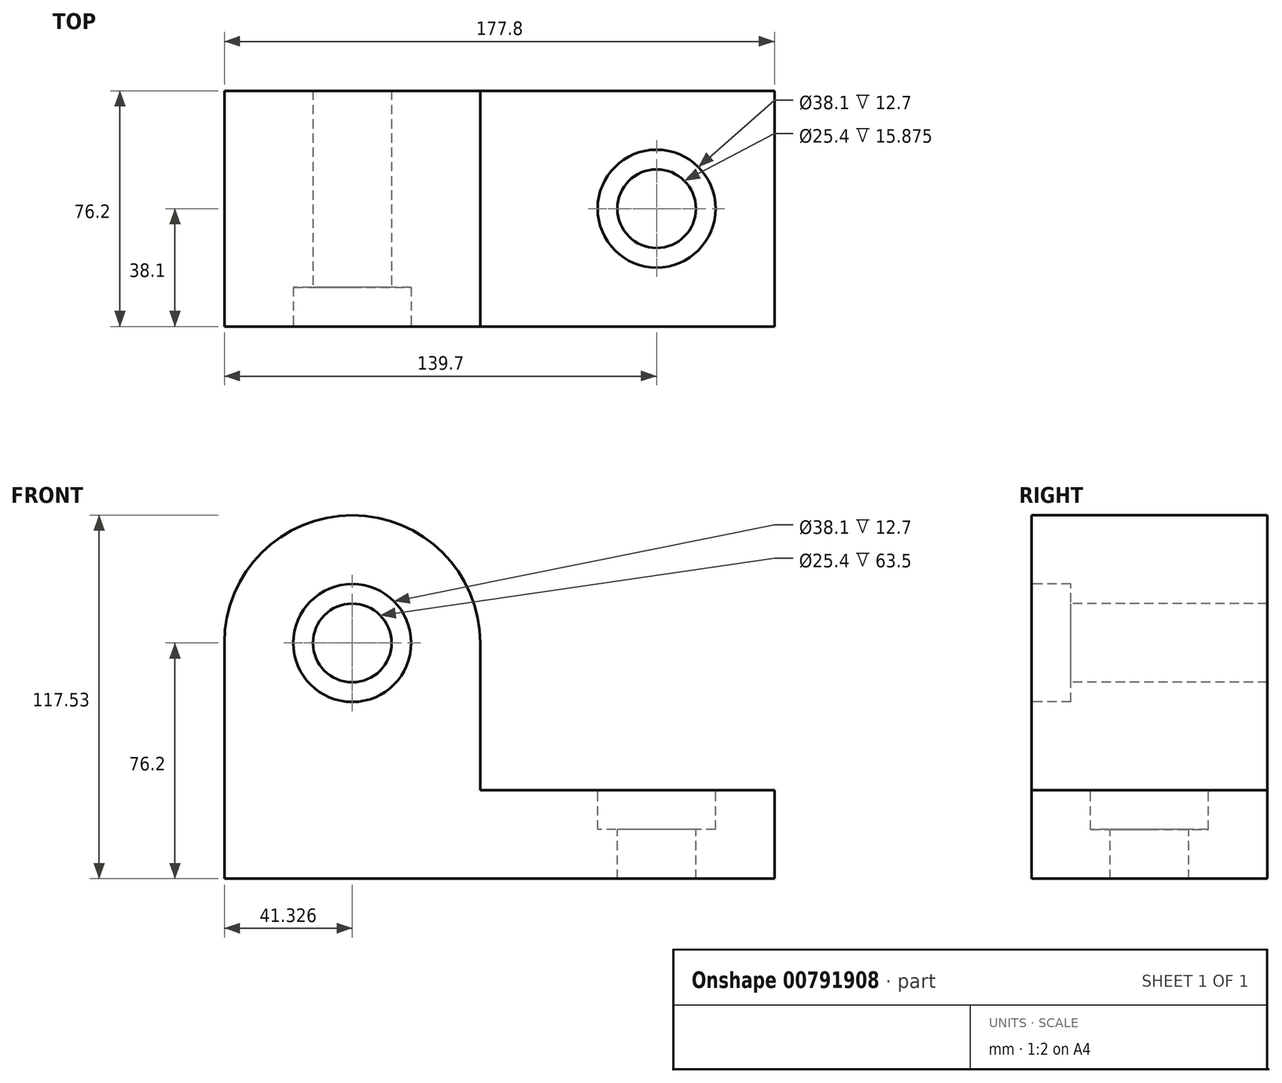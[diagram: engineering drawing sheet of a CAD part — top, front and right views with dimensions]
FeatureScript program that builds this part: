
annotation { "Feature Type Name" : "Feature", "Feature Type Description" : "" }
export const myFeature = defineFeature(function(context is Context, id is Id, definition is map)
    precondition{}
    {
        {
            var Q0;
            Q0=qCreatedBy(makeId("Front.planeOp"),FACE);
            var sketch = newSketch(context, id + "F0", { "sketchPlane" : qUnion([Q0])});
            skLineSegment(sketch, "E0", {"start": v(0, 0) * mm, "end": v(177.8, 0) * mm});
            skLineSegment(sketch, "E1", {"start": v(0, 0) * mm, "end": v(0, 139.7) * mm});
            skLineSegment(sketch, "E2", {"start": v(177.8, 0) * mm, "end": v(177.8, 28.58) * mm});
            skLineSegment(sketch, "E3", {"start": v(0, 0) * mm, "end": v(0, 76.2) * mm, "construction": true});
            skArc(sketch, "E4", {"start": v(82.65, 76.2) * mm, "mid": v(41.33, 117.53) * mm, "end": v(0, 76.2) * mm});
            skLineSegment(sketch, "E5", {"start": v(82.65, 76.2) * mm, "end": v(82.65, 28.58) * mm});
            skLineSegment(sketch, "E6", {"start": v(82.65, 28.58) * mm, "end": v(177.8, 28.58) * mm});
            skSolve(sketch);
        }
        {
            var Q0;
            {var subQ2=sQuery(id+"F0.wireOp",EDGE,"E0");Q0=makeQuery(id+"F0.imprint","IMPRINT",FACE,{"disambiguationData":[TD([[makeQuery(id+"F0.imprint","IMPRINT",EDGE,{"derivedFrom":subQ2}),1.0]])]});}
            extrude(context, id + "F1", {"entities" : qUnion([Q0]), "depth" : 76.2 * mm, "offsetDistance" : 25.4 * mm});
        }
        {
            var Q0;
            Q0=makeQuery(id+"F1.opExtrude","CAP_FACE",FACE,{"disambiguationData":[OSD([sQuery(id+"F0.wireOp",EDGE,"E0"),sQuery(id+"F0.wireOp",EDGE,"E1"),sQuery(id+"F0.wireOp",EDGE,"E2"),sQuery(id+"F0.wireOp",EDGE,"E4"),sQuery(id+"F0.wireOp",EDGE,"E5"),sQuery(id+"F0.wireOp",EDGE,"E6")])],"isStart":false});
            var sketch = newSketch(context, id + "F2", { "sketchPlane" : qUnion([Q0])});
            skLineSegment(sketch, "E7", {"start": v(0, 76.2) * mm, "end": v(82.65, 76.2) * mm, "construction": true});
            skLineSegment(sketch, "E8", {"start": v(41.33, 117.53) * mm, "end": v(41.33, 0) * mm, "construction": true});
            skCircle(sketch, "E9", {"center": v(41.33, 76.2) * mm, "radius": 19.05 * mm});
            skSolve(sketch);
        }
        {
            var Q0;
            Q0=makeQuery(id+"F2.imprint","IMPRINT",FACE,{"disambiguationData":[TD([[makeQuery(id+"F2.imprint","IMPRINT",EDGE,{"derivedFrom":sQuery(id+"F2.wireOp",EDGE,"E9")}),1.0]])]});
            extrude(context, id + "F3", {"entities" : qUnion([Q0]), "operationType" : NewBodyOperationType.REMOVE, "oppositeDirection" : true, "depth" : 12.7 * mm, "offsetDistance" : 25.4 * mm});
        }
        {
            var Q0;
            Q0=makeQuery(id+"F1.opExtrude","CAP_FACE",FACE,{"disambiguationData":[OSD([sQuery(id+"F0.wireOp",EDGE,"E0"),sQuery(id+"F0.wireOp",EDGE,"E1"),sQuery(id+"F0.wireOp",EDGE,"E2"),sQuery(id+"F0.wireOp",EDGE,"E4"),sQuery(id+"F0.wireOp",EDGE,"E5"),sQuery(id+"F0.wireOp",EDGE,"E6")])],"isStart":false});
            var sketch = newSketch(context, id + "F4", { "sketchPlane" : qUnion([Q0])});
            skLineSegment(sketch, "E10", {"start": v(41.33, 117.53) * mm, "end": v(41.33, 0) * mm, "construction": true});
            skLineSegment(sketch, "E11", {"start": v(0, 76.2) * mm, "end": v(82.65, 76.2) * mm, "construction": true});
            skCircle(sketch, "E12", {"center": v(41.33, 76.2) * mm, "radius": 12.7 * mm});
            skSolve(sketch);
        }
        {
            var Q0;
            Q0=makeQuery(id+"F4.imprint","IMPRINT",FACE,{"disambiguationData":[TD([[makeQuery(id+"F4.imprint","IMPRINT",EDGE,{"derivedFrom":sQuery(id+"F4.wireOp",EDGE,"E12")}),1.0]])]});
            extrude(context, id + "F5", {"entities" : qUnion([Q0]), "operationType" : NewBodyOperationType.REMOVE, "endBound" : BoundingType.UP_TO_NEXT, "oppositeDirection" : true, "depth" : 25.4 * mm, "offsetDistance" : 25.4 * mm});
        }
        {
            var Q0;
            Q0=makeQuery(id+"F3.boolean.opBoolean","COPY",FACE,{"derivedFrom":makeQuery(id+"F3.opExtrude","CAP_FACE",FACE,{"disambiguationData":[OSD([sQuery(id+"F2.wireOp",EDGE,"E9")])],"isStart":false})});
            var sketch = newSketch(context, id + "F6", { "sketchPlane" : qUnion([Q0])});
            skCircle(sketch, "E13", {"center": v(41.33, 76.2) * mm, "radius": 12.7 * mm});
            skSolve(sketch);
        }
        {
            var Q0;
            Q0 = qSketchRegion(id + "F6", true);
            extrude(context, id + "F7", {"entities" : qUnion([Q0]), "operationType" : NewBodyOperationType.REMOVE, "endBound" : BoundingType.UP_TO_NEXT, "oppositeDirection" : true, "depth" : 25.4 * mm, "offsetDistance" : 25.4 * mm});
        }
        {
            var Q0;
            Q0=makeQuery(id+"F1.opExtrude","SWEPT_FACE",FACE,{"disambiguationData":[OSD([sQuery(id+"F0.wireOp",EDGE,"E6")])]});
            var sketch = newSketch(context, id + "F8", { "sketchPlane" : qUnion([Q0])});
            skLineSegment(sketch, "E14", {"start": v(177.8, -38.1) * mm, "end": v(139.7, -38.1) * mm, "construction": true});
            skCircle(sketch, "E15", {"center": v(139.7, -38.1) * mm, "radius": 19.05 * mm});
            skSolve(sketch);
        }
        {
            var Q0;
            Q0=makeQuery(id+"F8.imprint","IMPRINT",FACE,{"disambiguationData":[TD([[makeQuery(id+"F8.imprint","IMPRINT",EDGE,{"derivedFrom":sQuery(id+"F8.wireOp",EDGE,"E15")}),1.0]])]});
            extrude(context, id + "F9", {"entities" : qUnion([Q0]), "operationType" : NewBodyOperationType.REMOVE, "oppositeDirection" : true, "depth" : 12.7 * mm, "offsetDistance" : 25.4 * mm});
        }
        {
            var Q0;
            Q0=makeQuery(id+"F9.boolean.opBoolean","COPY",FACE,{"derivedFrom":makeQuery(id+"F9.opExtrude","CAP_FACE",FACE,{"disambiguationData":[OSD([sQuery(id+"F8.wireOp",EDGE,"E15")])],"isStart":false})});
            var sketch = newSketch(context, id + "F10", { "sketchPlane" : qUnion([Q0])});
            skCircle(sketch, "E16", {"center": v(139.7, -38.1) * mm, "radius": 12.7 * mm});
            skSolve(sketch);
        }
        {
            var Q0;
            Q0=makeQuery(id+"F10.imprint","IMPRINT",FACE,{"disambiguationData":[TD([[makeQuery(id+"F10.imprint","IMPRINT",EDGE,{"derivedFrom":sQuery(id+"F10.wireOp",EDGE,"E16")}),1.0]])]});
            extrude(context, id + "F11", {"entities" : qUnion([Q0]), "operationType" : NewBodyOperationType.REMOVE, "endBound" : BoundingType.UP_TO_NEXT, "oppositeDirection" : true, "depth" : 25.4 * mm, "offsetDistance" : 25.4 * mm});
        }
    });
